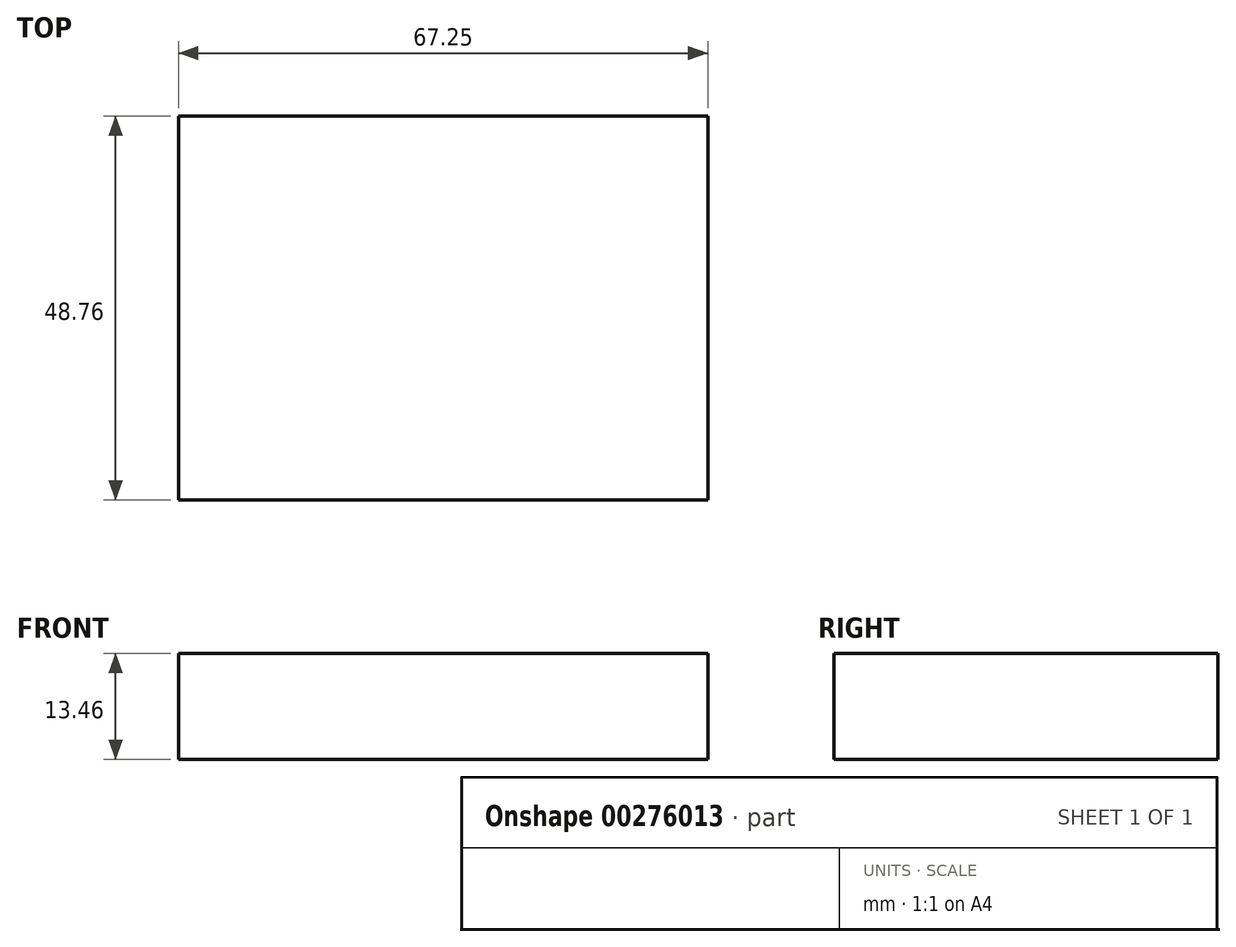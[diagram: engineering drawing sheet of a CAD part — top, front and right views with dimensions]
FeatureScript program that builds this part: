
annotation { "Feature Type Name" : "Feature", "Feature Type Description" : "" }
export const myFeature = defineFeature(function(context is Context, id is Id, definition is map)
    precondition{}
    {
        {
            var Q0;
            Q0=qCreatedBy(makeId("Top.planeOp"),FACE);
            var sketch = newSketch(context, id + "F0", { "sketchPlane" : qUnion([Q0])});
            skLineSegment(sketch, "E0.bottom", {"start": v(-68.3, 9.05) * mm, "end": v(-1.06, 9.05) * mm});
            skLineSegment(sketch, "E0.top", {"start": v(-68.3, -39.71) * mm, "end": v(-1.06, -39.71) * mm});
            skLineSegment(sketch, "E0.left", {"start": v(-68.3, 9.05) * mm, "end": v(-68.3, -39.71) * mm});
            skLineSegment(sketch, "E0.right", {"start": v(-1.06, 9.05) * mm, "end": v(-1.06, -39.71) * mm});
            skSolve(sketch);
        }
        {
            var Q0;
            Q0 = qSketchRegion(id + "F0", true);
            extrude(context, id + "F1", {"entities" : qUnion([Q0]), "depth" : 13.46 * mm});
        }
    });
